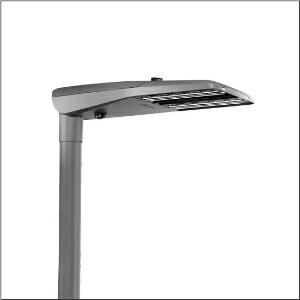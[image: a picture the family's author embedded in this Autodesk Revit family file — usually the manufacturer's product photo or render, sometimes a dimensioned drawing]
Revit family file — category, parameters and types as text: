
# Revit family: streetlight_sl_11_iq_midi___st0_5a_5xc3b51y08le_54cc
name_source: partatom
category: Lighting Fixtures
units: mm (PartAtom-declared; Revit-internal decimal feet)

## family parameters
Cut with Voids When Loaded = No
Host = Face
Light Source = No
Part Type = Normal
Room Calculation Point = No
Round Connector Dimension = Use Diameter
Shared = No

## types (1)
- --- (1 x LED, 9120 lm, 59.4 W, 3000K)
    Apparent Load = 59 VA
    CIE Flux Codes = 43 74 97 100 100
    Color Rendering = 70
    Color Temperature = 3000K
    Default Elevation = 1800 mm
    Description = Streetlight SL 11 iQ midi, mast luminaire, primary light control with 3 zone facetted reflector, of plastic, silver coated, highly specular, primary optical cover: cover, of PMMA, transparent, light distribution: ST0.5a, light emission: direct distribution, primary light characteristic: asymmetric, installation type: post-top, side-entry, LED, High Power LED, rated luminous flux: 9.120lm, luminous efficacy: 154lm/W, light colour: 730, colour temperature: 3000K, control: presetting dimming logarithmic, Street-Remote, Auto-Match, Temp-Guard, Lumen-Switch, Night-Set, Smart-Wire, Light-Fading, Desk-Remote (wireless, voltage-free reading and setting of iQ features in the workshop via application-optimized NFC function/RFID function), optimised constant luminous flux control (CLO 2.0), with cable H07RN-F 5x 1.5mm², mains connection: 230..240V, AC, 50/60Hz, connection cable pre-assembled, cable length: 8,5m, start of lifetime: 59W, end of service life: 62W, reduction: 29W, luminaire housing, of diecast aluminium, powder-coated, Siteco® metallic grey (DB 702S), please order mast flange separately, inclination adjustable without tools: 0°, 5°, 10°, 15° (post-top) | 0°, -5°, -10°, -15° (side-entry), sealing non-destructively replaceable, multi-level sealing system, length: 780mm, width: 376mm, height: 118mm, mast flange for spigot size: 42mm (side-entry): 5XC10008XM4, 60/48mm (side-entry/post-top): 5XC10108XM2, 76/60mm (side-entry/post-top): 5XC10108XM1, equipment: standard, Smart Interface below and above, protection rating (complete): IP66, insulation class (complete): insulation class II (safety insulation), certification: CE, ENEC, VDE, UKCA, impact resistance: IK09, permissible operating ambient temperature for outdoor applications: -25..+50°C, standard-compliant lighting for roads and squares, Environmental Product Declaration (EPD) tested and certified by an independent institute, packaging unit: 1 piece

Light Distribution: ST0.5a
    Height = 118 mm
    Lamp = 1 x LED
    Lamp Light Flux = 9120 lm
    Lamp Power = 59.4 W
    Lamp count = 1
    Length = 780 mm
    Luminous efficacy = 154 lm/W
    Manufacturer = Siteco
    ModVariant = No
    Model = 5XC3B51Y08LE
    Number of Poles = 1
    OnlyDefault = Yes
    Power Factor = 1
    Product Name = Streetlight SL 11 iQ midi | ST0.5a
    Product group = mast luminaire | pylon top
    ProductGroupID = 6100
    Protection Class = Protection class II
    Protection Degree = IP 66
    RLX_Detail_Level = 1
    RLX_Emergency_Light_Flux = 0 lm
    RLX_Emergency_Type = 0
    RLX_Emergency_Type_DB = No
    RlxData = <blob elided: 74229 chars, md5=51cfbca2>
    Socket = socket
    Standby Power = 0 W
    System Light Flux = 9120 lm
    System Power = 59 W
    Type Comments = factory setting: luminous flux: 100 % | dim-lin: 254 | 521 mA
    Type Image = l_1004429.jpg
    URL = http://relux.com
    VarID = @adj_064219
    Voltage = 0 V
    Weight = 0.00 kg
    Width = 376 mm

## geometry (parser evidence)
native form markers: Blend x4, Sweep x11
no freeform markers — native parametric forms only
